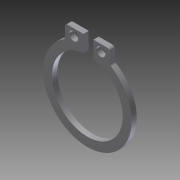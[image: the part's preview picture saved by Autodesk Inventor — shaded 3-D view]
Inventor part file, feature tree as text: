
AUTODESK INVENTOR PART (.ipt)
format: ipt  version: 2012 (Build 160160000, 160)  size: 110,080 bytes
history: native  units: in
note: dims shown in document units (in); Inventor stores cm internally (conversion verified against a paired STEP export)
features: extrude x1, sketch x1
ambient origin geometry x8: Origin, YZ Plane, XZ Plane, XY Plane, X Axis, Y Axis, Z Axis, Center Point
bodies: Solid1 (feature_tree)
feature tree (2):
  extrude  "Extrusion1"  Depth=0.0591in
  sketch  "Sketch1"  dims[d0=0.4724in d3=0.0591in d4=0.0591in d5=0.3in d6=0.0669in d7=0.0295in d8=0.0295in d9=0.0197in d10=0.0354in d11=0.0in d12=0.0197in d13=0.0197in d14=0.2953in]
